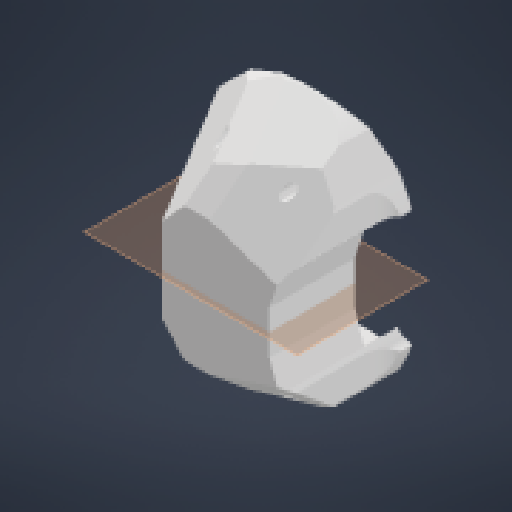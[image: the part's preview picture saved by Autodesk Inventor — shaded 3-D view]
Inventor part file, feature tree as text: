
AUTODESK INVENTOR PART (.ipt)
format: ipt  version: 2024 (Build 280153000, 153)  size: 312,320 bytes
history: native  units: in
note: dims shown in document units (in); Inventor stores cm internally (conversion verified against a paired STEP export)
features: chamfer x6, projected_geometry x6, extrude x4, sketch x4, reference x3, other x2
ambient origin geometry x8: Origin, YZ Plane, XZ Plane, XY Plane, X Axis, Y Axis, Z Axis, Center Point
bodies: Solid1 (feature_tree)
feature tree (25):
  extrude  "Extrusion1"  Depth=3.719in TaperAngle=0.0deg
  extrude  "Extrusion2"  Depth=1.0in
  extrude  "Extrusion3"  Depth=0.1875in
  chamfer  "Chamfer1"  Distance=0.3125in Angle=105.0deg
  extrude  "Extrusion4"  Depth=0.3125in TaperAngle=105.0deg
  chamfer  "Chamfer2"  Distance=0.5625in Angle=105.0deg
  chamfer  "Chamfer4"  [1 undecoded]
  chamfer  "Chamfer5"  [1 undecoded]
  chamfer  "Chamfer6"  [1 undecoded]
  chamfer  "Chamfer7"  [1 undecoded]
  sketch  "Sketch2"  dims[d0=0.5394in d1=0.0in d2=3.719in d3=0.0in]
  reference  "Reference2"
  reference  "Reference3"
  reference  "Reference4"
  sketch  "Sketch3"  dims[d4=1.378in d5=0.0in d6=1.0in d7=0.125in d8=0.4288in]
  projected_geometry  "Projected Loop1"
  sketch  "Sketch4"  dims[d9=4.878in d10=0.0in d12=0.1875in d13=0.125in d14=0.6528in d18=0.3125in d19=0.125in d20=105.0deg]
  projected_geometry  "Projected Loop2"
  sketch  "Sketch5"  dims[d21=0.3125in d22=0.125in d23=105.0deg d24=0.3125in d25=0.125in d26=105.0deg d27=0.5625in d28=0.125in d29=105.0deg]
  projected_geometry  "Projected Loop3"
  projected_geometry  "Projected Loop4"
  projected_geometry  "Projected Loop5"
  projected_geometry  "Projected Loop6"
  other  "Assembly5"
  other  "Camera_Baseplate:1"
note: 4 required parameter values undecoded (feature->parameter linkage not recoverable at this tier; creation-order binding heuristic only, values carry confidence <= 0.55)
